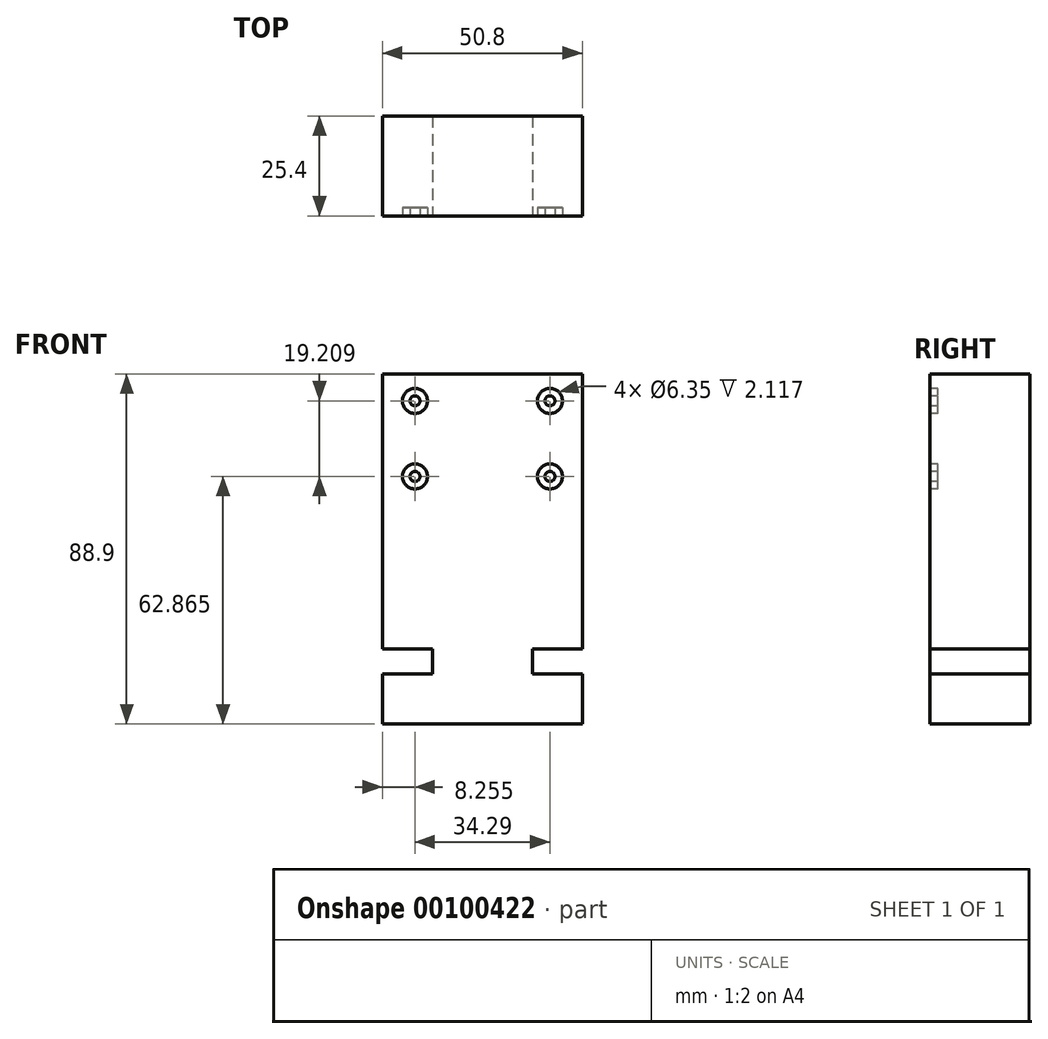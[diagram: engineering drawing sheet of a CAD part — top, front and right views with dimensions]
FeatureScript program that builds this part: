
annotation { "Feature Type Name" : "Feature", "Feature Type Description" : "" }
export const myFeature = defineFeature(function(context is Context, id is Id, definition is map)
    precondition{}
    {
        {
            var Q0;
            Q0=qCreatedBy(makeId("Front.planeOp"),FACE);
            var sketch = newSketch(context, id + "F0", { "sketchPlane" : qUnion([Q0])});
            skLineSegment(sketch, "E0", {"start": v(0, 0) * mm, "end": v(50.8, 0) * mm});
            skLineSegment(sketch, "E1", {"start": v(50.8, 0) * mm, "end": v(50.8, -69.85) * mm});
            skLineSegment(sketch, "E2", {"start": v(50.8, -69.85) * mm, "end": v(38.1, -69.85) * mm});
            skLineSegment(sketch, "E3", {"start": v(38.1, -69.85) * mm, "end": v(38.1, -76.2) * mm});
            skLineSegment(sketch, "E4", {"start": v(38.1, -76.2) * mm, "end": v(50.8, -76.2) * mm});
            skLineSegment(sketch, "E5", {"start": v(50.8, -76.2) * mm, "end": v(50.8, -88.9) * mm});
            skLineSegment(sketch, "E6", {"start": v(50.8, -88.9) * mm, "end": v(0, -88.9) * mm});
            skLineSegment(sketch, "E7", {"start": v(0, -88.9) * mm, "end": v(0, -76.2) * mm});
            skLineSegment(sketch, "E8", {"start": v(0, -76.2) * mm, "end": v(12.7, -76.2) * mm});
            skLineSegment(sketch, "E9", {"start": v(12.7, -76.2) * mm, "end": v(12.7, -69.85) * mm});
            skLineSegment(sketch, "E10", {"start": v(12.7, -69.85) * mm, "end": v(0, -69.85) * mm});
            skLineSegment(sketch, "E11", {"start": v(0, -69.85) * mm, "end": v(0, 0) * mm});
            skSolve(sketch);
        }
        {
            var Q0;
            Q0 = qSketchRegion(id + "F0", true);
            extrude(context, id + "F1", {"entities" : qUnion([Q0]), "oppositeDirection" : true, "depth" : 25.4 * mm});
        }
        {
            var Q0;
            Q0=makeQuery(id+"F1.opExtrude","CAP_FACE",FACE,{"disambiguationData":[OSD([sQuery(id+"F0.wireOp",EDGE,"E0"),sQuery(id+"F0.wireOp",EDGE,"E1"),sQuery(id+"F0.wireOp",EDGE,"E2"),sQuery(id+"F0.wireOp",EDGE,"E3"),sQuery(id+"F0.wireOp",EDGE,"E4"),sQuery(id+"F0.wireOp",EDGE,"E5"),sQuery(id+"F0.wireOp",EDGE,"E6"),sQuery(id+"F0.wireOp",EDGE,"E7"),sQuery(id+"F0.wireOp",EDGE,"E8"),sQuery(id+"F0.wireOp",EDGE,"E9"),sQuery(id+"F0.wireOp",EDGE,"E10"),sQuery(id+"F0.wireOp",EDGE,"E11")])],"isStart":true});
            var sketch = newSketch(context, id + "F2", { "sketchPlane" : qUnion([Q0])});
            skCircle(sketch, "E12", {"center": v(8.26, -6.83) * mm, "radius": 1.27 * mm});
            skCircle(sketch, "E13", {"center": v(42.55, -6.83) * mm, "radius": 1.27 * mm});
            skLineSegment(sketch, "E14", {"start": v(8.26, -6.83) * mm, "end": v(0, -6.83) * mm});
            skLineSegment(sketch, "E15", {"start": v(42.55, -6.83) * mm, "end": v(50.8, -6.83) * mm});
            skCircle(sketch, "E16", {"center": v(8.26, -6.83) * mm, "radius": 3.18 * mm});
            skCircle(sketch, "E17", {"center": v(42.55, -6.83) * mm, "radius": 3.18 * mm});
            skLineSegment(sketch, "E18", {"start": v(42.55, -8.1) * mm, "end": v(42.55, -24.77) * mm});
            skCircle(sketch, "E19", {"center": v(42.55, -26.04) * mm, "radius": 1.27 * mm});
            skLineSegment(sketch, "E20", {"start": v(42.55, -26.04) * mm, "end": v(42.55, -24.77) * mm});
            skCircle(sketch, "E21", {"center": v(42.55, -26.04) * mm, "radius": 3.18 * mm});
            skCircle(sketch, "E22", {"center": v(8.26, -26.04) * mm, "radius": 1.27 * mm});
            skCircle(sketch, "E23", {"center": v(8.26, -26.04) * mm, "radius": 3.18 * mm});
            skSolve(sketch);
        }
        {
            var Q0;
            Q0 = qSketchRegion(id + "F2", true);
            extrude(context, id + "F3", {"entities" : qUnion([Q0]), "operationType" : NewBodyOperationType.REMOVE, "oppositeDirection" : true, "depth" : 2.12 * mm});
        }
    });
